# Revit family: 71 High Head series grinder Vertical dsc
name_source: partatom
category: Mechanical Equipment
revit_build: Autodesk Revit 2013 (Build: 20120221_2030(x64)
units: mm (PartAtom-declared; Revit-internal decimal feet)

## types (14) — shared parameters
Assembly Code = D2010900
Connector Description = 2" NPT
Default Elevation = 0"
Description = Commercial Grinder Pumps
Discharge Diameter = 2
Discharge Radius = 1"
Flow @ 3' = 104 GPM
Height = 28 1/8"
Hertz = 60
Impeller Type = Bronze Vortex
Installation Type = Floor Mounted
Insulation = Class F
Lead Wires Insulation = Class F
Length = 15"
Manufacturer = Zoeller
Masterformat Number = 43 26 13
Masterformat Title = Submersible Grinder Pumps
Material = Cast Iron-Zoeller-Powder Coated Epoxy
Max. Stator Temp. = 311 °F
Max. Water Temp. = 104 °F
Moisture Detection = Moisture Sensing Probes (Requires a circuit in control panel to function)
Motor Shaft = 416 S.S.
Motor Thermal Shutoff = Thermal Sensors with Automatic Reset (Requires a circuit in control panel to function)
Motor Type = Submersible
Omniclass Table 23 Code = 23.60.30.21
Omniclass Table 23 Title = Pumps
Operation = Non-Automatic
Power Cord = #12-4 SO (Models with a FLA greater than 20 amps use #8-4 gauge power cord)
Price = Prices may vary. Please consult Manufacturer Representative for most up-to-date price list.
Product Page URL = http://www.zoellerengprod.com
RPM = 3450
Service Factor = 1.2
Shaft Seal Lower (Options) = Carbon/Silicon Carbide, Silicon Carbide/Silicon Carbide
Shaft Seal Lower Standard = Carbon/Ceramic
Shaft Seal Upper (Options) = Carbon/Silicon Carbide Silicon Carbide/Silicon Carbide
Shaft Seal Upper Standard = Carbon/Ceramic
Shipping Weight = 245 lbs (111 kg)
Tandem Seals = Standard
Type SOW Power Cord Length = 300"
URL = http://www.zoellerengprod.com
Warranty Information = 36 Months (Limited)
Waste Connection = Yes
Width = 11 3/4"

## per-type parameters (varying)
| type | Apparent Load | Full Load Amps | Locked Rotor Amps | Maximum KW Input | Model | Motor | Motor Design Letter | NEC Locked Rotor Code | Phase | Type | Voltage |
| 7111 - 2" 230V 1Ph | 6440 VA | 28 A | 132 A | 6.4 | 7111-2" | 5.0 BHP | NEMA L (1 Ph), NEMA B (3 Ph) | G (1 Ph), H (3 Ph) | 1 | Permanent Split Capacitor | 230 V |
| 7110 - 2" 230V 1Ph | 5428 VA | 24 A | 132 A | 5.3 | 7110-2" | 3.0 BHP | NEMA L (1 Ph), NEMA B (3 Ph) | M (1 Ph), G (3 Ph) | 1 | Permanent Split Capacitor | 230 V |
| 7110 - 2" 208V 3Ph | 3598 VA | 17 A | 66 A | 5.3 | 7110-2" | 3.0 BHP | NEMA L (1 Ph), NEMA B (3 Ph) | M (1 Ph), G (3 Ph) | 3 | 3 Phase | 208 V |
| 7110 - 2" 230V 3Ph | 3473 VA | 15 A | 57 A | 5.3 | 7110-2" | 3.0 BHP | NEMA L (1 Ph), NEMA B (3 Ph) | M (1 Ph), G (3 Ph) | 3 | 3 Phase | 230 V |
| 7110 - 2" 460V 3Ph | 3450 VA | 8 A | 29 A | 5.3 | 7110-2" | 3.0 BHP | NEMA L (1 Ph), NEMA B (3 Ph) | M (1 Ph), G (3 Ph) | 3 | 3 Phase | 460 V |
| 7110 - 2" 575V 3Ph | 3450 VA | 6 A | 25 A | 5.3 | 7110-2" | 3.0 BHP | NEMA L (1 Ph), NEMA B (3 Ph) | M (1 Ph), G (3 Ph) | 3 | 3 Phase | 575 V |
| 7111 - 2" 208V 3Ph | 4306 VA | 21 A | 94 A | 6.4 | 7111-2" | 5.0 BHP | NEMA L (1 Ph), NEMA B (3 Ph) | G (1 Ph), H (3 Ph) | 3 | 3 Phase | 208 V |
| 7111 - 2" 230V 3Ph | 4140 VA | 18 A | 82 A | 6.4 | 7111-2" | 5.0 BHP | NEMA L (1 Ph), NEMA B (3 Ph) | G (1 Ph), H (3 Ph) | 3 | 3 Phase | 230 V |
| 7111 - 2" 460V 3Ph | 4140 VA | 9 A | 41 A | 6.4 | 7111-2" | 5.0 BHP | NEMA L (1 Ph), NEMA B (3 Ph) | G (1 Ph), H (3 Ph) | 3 | 3 Phase | 460 V |
| 7111 - 2" 575V 3Ph | 4140 VA | 7 A | 36 A | 6.4 | 7111-2" | 5.0 BHP | NEMA L (1 Ph), NEMA B (3 Ph) | G (1 Ph), H (3 Ph) | 3 | 3 Phase | 575 V |
| 7112 - 2" 208V 3Ph | 5262 VA | 25 A | 94 A | 8.0 | 7112-2" | 7.5 BHP | NEMA B (3 Ph) | D | 3 | 3 Phase | 208 V |
| 7112 - 2" 230V 3Ph | 5060 VA | 22 A | 82 A | 8.0 | 7112-2" | 7.5 BHP | NEMA B (3 Ph) | D | 3 | 3 Phase | 230 V |
| 7112 - 2" 460V 3Ph | 5060 VA | 11 A | 41 A | 8.0 | 7112-2" | 7.5 BHP | NEMA B (3 Ph) | D | 3 | 3 Phase | 460 V |
| 7112 - 2" 575V 3Ph | 5175 VA | 9 A | 36 A | 8.0 | 7112-2" | 7.5 BHP | NEMA B (3 Ph) | D | 3 | 3 Phase | 575 V |

## geometry (parser evidence)
native form markers: Blend x6, Sweep x1
no freeform markers — native parametric forms only
